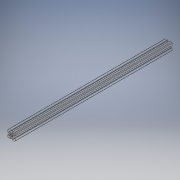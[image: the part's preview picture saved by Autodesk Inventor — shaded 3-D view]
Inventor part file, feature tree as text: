
AUTODESK INVENTOR PART (.ipt)
format: ipt  version: 2019 (Build 230136000, 136)  size: 233,472 bytes
history: native  units: in
note: dims shown in document units (in); Inventor stores cm internally (conversion verified against a paired STEP export)
features: plane x1, extrude x1, sketch x1
ambient origin geometry x8: Origin, YZ Plane, XZ Plane, XY Plane, X Axis, Y Axis, Z Axis, Center Point
bodies: Solid1 (feature_tree)
feature tree (3):
  plane  "Work Plane1"
  extrude  "Extrusion1"  [1 undecoded]
  sketch  "Sketch1"  dims[d0=32.5in d1=0.0in]
note: 1 required parameter value undecoded (feature->parameter linkage not recoverable at this tier; creation-order binding heuristic only, values carry confidence <= 0.55)
